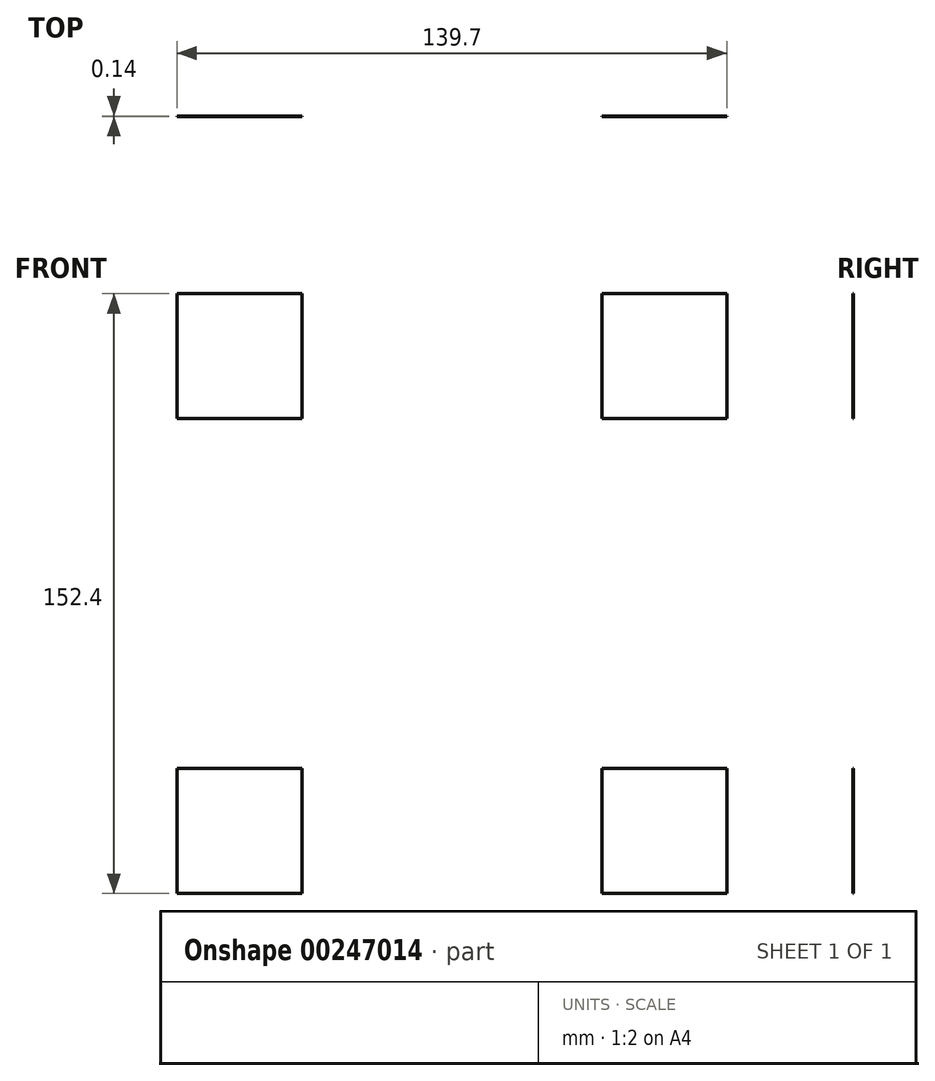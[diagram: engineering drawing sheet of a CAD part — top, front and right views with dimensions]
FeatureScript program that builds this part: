
annotation { "Feature Type Name" : "Feature", "Feature Type Description" : "" }
export const myFeature = defineFeature(function(context is Context, id is Id, definition is map)
    precondition{}
    {
        {
            var Q0;
            Q0=qCreatedBy(makeId("Front.planeOp"),FACE);
            var sketch = newSketch(context, id + "F0", { "sketchPlane" : qUnion([Q0])});
            skLineSegment(sketch, "E0.bottom", {"start": v(-128.03, 76.75) * mm, "end": v(125.97, 76.75) * mm});
            skLineSegment(sketch, "E0.top", {"start": v(-128.03, -75.65) * mm, "end": v(125.97, -75.65) * mm});
            skLineSegment(sketch, "E0.left", {"start": v(-128.03, 76.75) * mm, "end": v(-128.03, 25.95) * mm});
            skLineSegment(sketch, "E0.right", {"start": v(125.97, 76.75) * mm, "end": v(125.97, 25.6) * mm});
            skLineSegment(sketch, "E1", {"start": v(-70.88, 76.75) * mm, "end": v(-70.88, -75.65) * mm});
            skLineSegment(sketch, "E2", {"start": v(68.82, 76.75) * mm, "end": v(68.82, -75.65) * mm});
            skLineSegment(sketch, "E3", {"start": v(-39.13, 45) * mm, "end": v(-70.88, 45) * mm});
            skLineSegment(sketch, "E4", {"start": v(-39.13, -43.9) * mm, "end": v(-70.88, -43.9) * mm});
            skLineSegment(sketch, "E5", {"start": v(-39.13, 76.75) * mm, "end": v(-39.13, -75.65) * mm});
            skLineSegment(sketch, "E6", {"start": v(37.07, 45) * mm, "end": v(68.82, 45) * mm});
            skLineSegment(sketch, "E7", {"start": v(37.07, -43.9) * mm, "end": v(68.82, -43.9) * mm});
            skLineSegment(sketch, "E8", {"start": v(37.07, 76.75) * mm, "end": v(37.07, -75.65) * mm});
            skCircle(sketch, "E9", {"center": v(0, 0) * mm, "radius": 15.88 * mm});
            skLineSegment(sketch, "E10.bottom", {"start": v(-128.03, 25.95) * mm, "end": v(-86.76, 25.95) * mm});
            skLineSegment(sketch, "E10.top", {"start": v(-128.03, -24.85) * mm, "end": v(-86.76, -24.85) * mm});
            skLineSegment(sketch, "E10.right", {"start": v(-86.76, 25.95) * mm, "end": v(-86.76, -24.85) * mm});
            skLineSegment(sketch, "E11.trimOffspring", {"start": v(-128.03, -24.85) * mm, "end": v(-128.03, -75.65) * mm});
            skLineSegment(sketch, "E12.bottom", {"start": v(125.97, -25.2) * mm, "end": v(84.7, -25.2) * mm});
            skLineSegment(sketch, "E12.top", {"start": v(125.97, 25.6) * mm, "end": v(84.7, 25.6) * mm});
            skLineSegment(sketch, "E12.right", {"start": v(84.7, -25.2) * mm, "end": v(84.7, 25.6) * mm});
            skLineSegment(sketch, "E13.trimOffspring", {"start": v(125.97, -25.2) * mm, "end": v(125.97, -75.65) * mm});
            skSolve(sketch);
        }
        {
            var Q0;
            {var subQ4=sQuery(id+"F0.wireOp",EDGE,"E0.left");Q0=makeQuery(id+"F0.imprint","IMPRINT",FACE,{"disambiguationData":[TD([[makeQuery(id+"F0.imprint","IMPRINT",EDGE,{"derivedFrom":subQ4}),1.0]])]});}
            var Q1;
            {var subQ3=sQuery(id+"F0.wireOp",EDGE,"dv9NgrK8-mtO0-p72W-8hx8-IGgEpmCloeRB");Q1=makeQuery(id+"F0.imprint","IMPRINT",FACE,{"disambiguationData":[TD([[makeQuery(id+"F0.imprint","IMPRINT",EDGE,{"derivedFrom":subQ3}),1.0]])]});}
            var Q2;
            {var subQ4=sQuery(id+"F0.wireOp",EDGE,"E0.right");Q2=makeQuery(id+"F0.imprint","IMPRINT",FACE,{"disambiguationData":[TD([[makeQuery(id+"F0.imprint","IMPRINT",EDGE,{"derivedFrom":subQ4}),-1.0]])]});}
            var Q3;
            {var subQ3=sQuery(id+"F0.wireOp",EDGE,"w8YUugLR-fw0A-xvdc-tAc0-qzUKYsgOugrA");Q3=makeQuery(id+"F0.imprint","IMPRINT",FACE,{"disambiguationData":[TD([[makeQuery(id+"F0.imprint","IMPRINT",EDGE,{"derivedFrom":subQ3}),1.0]])]});}
            var Q4;
            {var subQ3=sQuery(id+"F0.wireOp",EDGE,"GDpQffIL-IsZD-Ed3l-nyGJ-e4jcA56aZtdY");Q4=makeQuery(id+"F0.imprint","IMPRINT",FACE,{"disambiguationData":[TD([[makeQuery(id+"F0.imprint","IMPRINT",EDGE,{"derivedFrom":subQ3}),-1.0]])]});}
            var Q5;
            {var subQ3=sQuery(id+"F0.wireOp",EDGE,"e1BejX3T-LJf1-kyOh-JE4F-RBOIruYoSUoQ");Q5=makeQuery(id+"F0.imprint","IMPRINT",FACE,{"disambiguationData":[TD([[makeQuery(id+"F0.imprint","IMPRINT",EDGE,{"derivedFrom":subQ3}),1.0]])]});}
            var Q6;
            {var subQ0=sQuery(id+"F0.wireOp",EDGE,"E3");Q6=makeQuery(id+"F0.imprint","IMPRINT",FACE,{"disambiguationData":[TD([[makeQuery(id+"F0.imprint","IMPRINT",EDGE,{"derivedFrom":subQ0}),1.0]])]});}
            var Q7;
            {var subQ0=sQuery(id+"F0.wireOp",EDGE,"E6");Q7=makeQuery(id+"F0.imprint","IMPRINT",FACE,{"disambiguationData":[TD([[makeQuery(id+"F0.imprint","IMPRINT",EDGE,{"derivedFrom":subQ0}),-1.0]])]});}
            var Q8;
            {var subQ3=sQuery(id+"F0.wireOp",EDGE,"e1BejX3T-LJf1-kyOh-JE4F-RBOIruYoSUoQ");Q8=makeQuery(id+"F0.imprint","IMPRINT",FACE,{"disambiguationData":[TD([[makeQuery(id+"F0.imprint","IMPRINT",EDGE,{"derivedFrom":subQ3}),-1.0]])]});}
            var Q9;
            {var subQ5=sQuery(id+"F0.wireOp",EDGE,"E4");Q9=makeQuery(id+"F0.imprint","IMPRINT",FACE,{"disambiguationData":[TD([[makeQuery(id+"F0.imprint","IMPRINT",EDGE,{"derivedFrom":subQ5}),1.0]])]});}
            var Q10;
            Q10=makeQuery(id+"F0.imprint","IMPRINT",FACE,{"disambiguationData":[TD([[makeQuery(id+"F0.imprint","IMPRINT",EDGE,{"derivedFrom":sQuery(id+"F0.wireOp",EDGE,"E9")}),-1.0]])]});
            var Q11;
            {var subQ5=sQuery(id+"F0.wireOp",EDGE,"E7");Q11=makeQuery(id+"F0.imprint","IMPRINT",FACE,{"disambiguationData":[TD([[makeQuery(id+"F0.imprint","IMPRINT",EDGE,{"derivedFrom":subQ5}),-1.0]])]});}
            var Q12;
            {var subQ5=sQuery(id+"F0.wireOp",EDGE,"E3");Q12=makeQuery(id+"F0.imprint","IMPRINT",FACE,{"disambiguationData":[TD([[makeQuery(id+"F0.imprint","IMPRINT",EDGE,{"derivedFrom":subQ5}),-1.0]])]});}
            var Q13;
            {var subQ5=sQuery(id+"F0.wireOp",EDGE,"E6");Q13=makeQuery(id+"F0.imprint","IMPRINT",FACE,{"disambiguationData":[TD([[makeQuery(id+"F0.imprint","IMPRINT",EDGE,{"derivedFrom":subQ5}),1.0]])]});}
            extrude(context, id + "F1", {"entities" : qUnion([Q0, Q1, Q2, Q3, Q4, Q5, Q6, Q7, Q8, Q9, Q10, Q11, Q12, Q13]), "depth" : 29 / 203.2 * mm});
        }
        {
            var Q0;
            {var subQ4=sQuery(id+"F0.wireOp",EDGE,"E0.left");Q0=makeQuery(id+"F0.imprint","IMPRINT",FACE,{"disambiguationData":[TD([[makeQuery(id+"F0.imprint","IMPRINT",EDGE,{"derivedFrom":subQ4}),1.0]])]});}
            var Q1;
            {var subQ4=sQuery(id+"F0.wireOp",EDGE,"E0.right");Q1=makeQuery(id+"F0.imprint","IMPRINT",FACE,{"disambiguationData":[TD([[makeQuery(id+"F0.imprint","IMPRINT",EDGE,{"derivedFrom":subQ4}),-1.0]])]});}
            extrude(context, id + "F2", {"entities" : qUnion([Q0, Q1]), "operationType" : NewBodyOperationType.REMOVE, "depth" : 60.32 * mm});
        }
        {
            var Q0;
            {var subQ0=sQuery(id+"F0.wireOp",EDGE,"E3");Q0=makeQuery(id+"F0.imprint","IMPRINT",FACE,{"disambiguationData":[TD([[makeQuery(id+"F0.imprint","IMPRINT",EDGE,{"derivedFrom":subQ0}),1.0]])]});}
            var Q1;
            {var subQ0=sQuery(id+"F0.wireOp",EDGE,"E6");Q1=makeQuery(id+"F0.imprint","IMPRINT",FACE,{"disambiguationData":[TD([[makeQuery(id+"F0.imprint","IMPRINT",EDGE,{"derivedFrom":subQ0}),-1.0]])]});}
            extrude(context, id + "F3", {"entities" : qUnion([Q0, Q1]), "operationType" : NewBodyOperationType.REMOVE, "depth" : 19.05 * mm});
        }
        {
            var Q0;
            {var subQ3=sQuery(id+"F0.wireOp",EDGE,"e1BejX3T-LJf1-kyOh-JE4F-RBOIruYoSUoQ");Q0=makeQuery(id+"F0.imprint","IMPRINT",FACE,{"disambiguationData":[TD([[makeQuery(id+"F0.imprint","IMPRINT",EDGE,{"derivedFrom":subQ3}),1.0]])]});}
            var Q1;
            Q1=makeQuery(id+"F0.imprint","IMPRINT",FACE,{"disambiguationData":[TD([[makeQuery(id+"F0.imprint","IMPRINT",EDGE,{"derivedFrom":sQuery(id+"F0.wireOp",EDGE,"E9")}),-1.0]])]});
            extrude(context, id + "F4", {"entities" : qUnion([Q0, Q1]), "operationType" : NewBodyOperationType.REMOVE, "depth" : 38.1 * mm});
        }
    });
